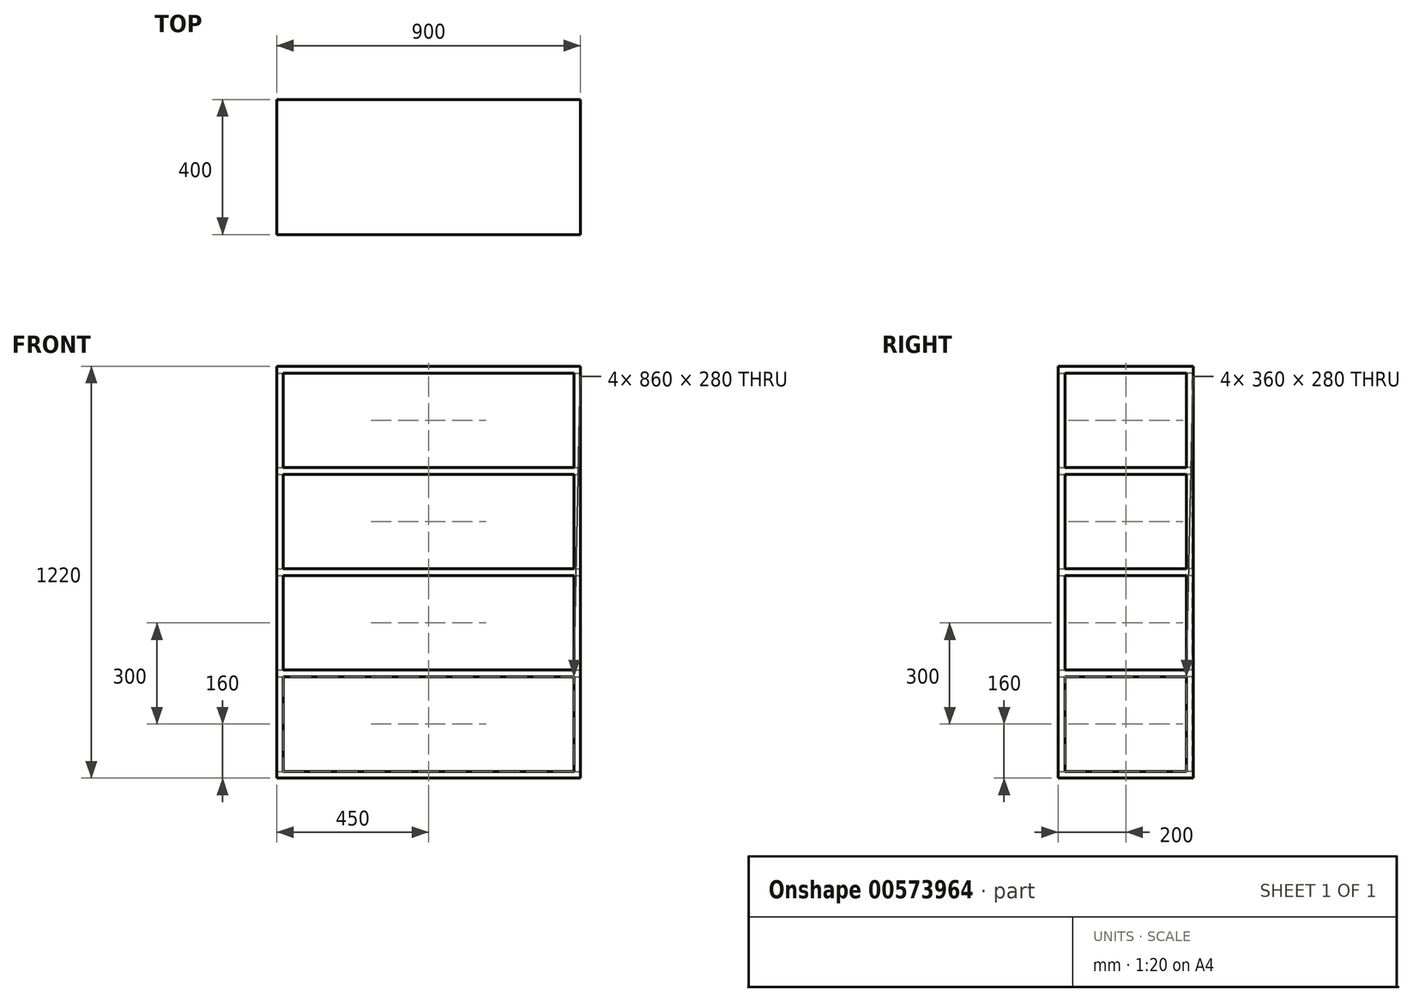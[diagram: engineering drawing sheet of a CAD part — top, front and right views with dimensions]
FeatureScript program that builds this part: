
annotation { "Feature Type Name" : "Feature", "Feature Type Description" : "" }
export const myFeature = defineFeature(function(context is Context, id is Id, definition is map)
    precondition{}
    {
        {
            var Q0;
            Q0=qCreatedBy(makeId("Top.planeOp"),FACE);
            cPlane(context, id + "F0", {"entities" : qUnion([Q0]), "cplaneType" : CPlaneType.OFFSET, "offset" : 300 * mm, "width" : 150 * mm, "height" : 150 * mm});
        }
        {
            var Q0;
            Q0=qCreatedBy(makeId("Top.planeOp"),FACE);
            cPlane(context, id + "F1", {"entities" : qUnion([Q0]), "cplaneType" : CPlaneType.OFFSET, "offset" : 600 * mm, "width" : 150 * mm, "height" : 150 * mm});
        }
        {
            var Q0;
            Q0=qCreatedBy(makeId("Top.planeOp"),FACE);
            cPlane(context, id + "F2", {"entities" : qUnion([Q0]), "cplaneType" : CPlaneType.OFFSET, "offset" : 900 * mm, "width" : 150 * mm, "height" : 150 * mm});
        }
        {
            var Q0;
            Q0=qCreatedBy(makeId("Top.planeOp"),FACE);
            cPlane(context, id + "F3", {"entities" : qUnion([Q0]), "cplaneType" : CPlaneType.OFFSET, "offset" : 1200 * mm, "width" : 150 * mm, "height" : 150 * mm});
        }
        {
            var Q0;
            Q0=qCreatedBy(makeId("Top.planeOp"),FACE);
            var sketch = newSketch(context, id + "F4", { "sketchPlane" : qUnion([Q0])});
            skLineSegment(sketch, "E0.bottom", {"start": v(450, 200) * mm, "end": v(-450, 200) * mm});
            skLineSegment(sketch, "E0.top", {"start": v(450, -200) * mm, "end": v(-450, -200) * mm});
            skLineSegment(sketch, "E0.left", {"start": v(450, 200) * mm, "end": v(450, -200) * mm});
            skLineSegment(sketch, "E0.right", {"start": v(-450, 200) * mm, "end": v(-450, -200) * mm});
            skPoint(sketch, "E0.middle", {"position": v(0, 0) * mm});
            skSolve(sketch);
        }
        {
            var Q0;
            Q0=qCreatedBy(id+"F0.planeOp",FACE);
            var sketch = newSketch(context, id + "F5", { "sketchPlane" : qUnion([Q0])});
            skPoint(sketch, "E1.middle", {"position": v(0, 0) * mm});
            skLineSegment(sketch, "E2", {"start": v(-448, 198) * mm, "end": v(-448, 180) * mm});
            skLineSegment(sketch, "E3", {"start": v(-448, 180) * mm, "end": v(-450, 180) * mm});
            skLineSegment(sketch, "E4", {"start": v(-448, 198) * mm, "end": v(-430, 198) * mm});
            skLineSegment(sketch, "E5", {"start": v(-430, 198) * mm, "end": v(-430, 200) * mm});
            skLineSegment(sketch, "E6", {"start": v(-448, -198) * mm, "end": v(-448, -180) * mm});
            skLineSegment(sketch, "E7", {"start": v(-448, -180) * mm, "end": v(-450, -180) * mm});
            skLineSegment(sketch, "E8", {"start": v(-448, -198) * mm, "end": v(-430, -198) * mm});
            skLineSegment(sketch, "E9", {"start": v(-430, -198) * mm, "end": v(-430, -200) * mm});
            skLineSegment(sketch, "E10", {"start": v(448, -198) * mm, "end": v(448, -180) * mm});
            skLineSegment(sketch, "E11", {"start": v(448, -180) * mm, "end": v(450, -180) * mm});
            skLineSegment(sketch, "E12", {"start": v(430, -198) * mm, "end": v(448, -198) * mm});
            skLineSegment(sketch, "E13", {"start": v(430, -200) * mm, "end": v(430, -198) * mm});
            skLineSegment(sketch, "E14", {"start": v(448, 198) * mm, "end": v(448, 180) * mm});
            skLineSegment(sketch, "E15", {"start": v(448, 180) * mm, "end": v(450, 180) * mm});
            skLineSegment(sketch, "E16", {"start": v(448, 198) * mm, "end": v(430, 198) * mm});
            skLineSegment(sketch, "E17", {"start": v(430, 198) * mm, "end": v(430, 200) * mm});
            skLineSegment(sketch, "E18", {"start": v(430, 200) * mm, "end": v(-430, 200) * mm});
            skLineSegment(sketch, "E19", {"start": v(-450, 180) * mm, "end": v(-450, -180) * mm});
            skLineSegment(sketch, "E20", {"start": v(450, 180) * mm, "end": v(450, -180) * mm});
            skLineSegment(sketch, "E21", {"start": v(430, -200) * mm, "end": v(-430, -200) * mm});
            skSolve(sketch);
        }
        {
            var Q0;
            Q0 = qSketchRegion(id + "F4", true);
            extrude(context, id + "F6", {"entities" : qUnion([Q0]), "depth" : 1220 * mm, "offsetDistance" : 25 * mm});
        }
        {
            var Q0;
            Q0 = qSketchRegion(id + "F5", true);
            extrude(context, id + "F7", {"entities" : qUnion([Q0]), "operationType" : NewBodyOperationType.REMOVE, "oppositeDirection" : true, "depth" : 280 * mm, "offsetDistance" : 25 * mm});
        }
        {
            var Q0;
            Q0=qCreatedBy(id+"F1.planeOp",FACE);
            var sketch = newSketch(context, id + "F8", { "sketchPlane" : qUnion([Q0])});
            skPoint(sketch, "E22.middle", {"position": v(0, 0) * mm});
            skLineSegment(sketch, "E23", {"start": v(-448, 198) * mm, "end": v(-448, 180) * mm});
            skLineSegment(sketch, "E24", {"start": v(-448, 180) * mm, "end": v(-450, 180) * mm});
            skLineSegment(sketch, "E25", {"start": v(-448, 198) * mm, "end": v(-430, 198) * mm});
            skLineSegment(sketch, "E26", {"start": v(-430, 198) * mm, "end": v(-430, 200) * mm});
            skLineSegment(sketch, "E27", {"start": v(-448, -198) * mm, "end": v(-448, -180) * mm});
            skLineSegment(sketch, "E28", {"start": v(-448, -180) * mm, "end": v(-450, -180) * mm});
            skLineSegment(sketch, "E29", {"start": v(-448, -198) * mm, "end": v(-430, -198) * mm});
            skLineSegment(sketch, "E30", {"start": v(-430, -198) * mm, "end": v(-430, -200) * mm});
            skLineSegment(sketch, "E31", {"start": v(448, -198) * mm, "end": v(448, -180) * mm});
            skLineSegment(sketch, "E32", {"start": v(448, -180) * mm, "end": v(450, -180) * mm});
            skLineSegment(sketch, "E33", {"start": v(430, -198) * mm, "end": v(448, -198) * mm});
            skLineSegment(sketch, "E34", {"start": v(430, -200) * mm, "end": v(430, -198) * mm});
            skLineSegment(sketch, "E35", {"start": v(448, 198) * mm, "end": v(448, 180) * mm});
            skLineSegment(sketch, "E36", {"start": v(448, 180) * mm, "end": v(450, 180) * mm});
            skLineSegment(sketch, "E37", {"start": v(448, 198) * mm, "end": v(430, 198) * mm});
            skLineSegment(sketch, "E38", {"start": v(430, 198) * mm, "end": v(430, 200) * mm});
            skLineSegment(sketch, "E39", {"start": v(430, 200) * mm, "end": v(-430, 200) * mm});
            skLineSegment(sketch, "E40", {"start": v(-450, 180) * mm, "end": v(-450, -180) * mm});
            skLineSegment(sketch, "E41", {"start": v(450, 180) * mm, "end": v(450, -180) * mm});
            skLineSegment(sketch, "E42", {"start": v(430, -200) * mm, "end": v(-430, -200) * mm});
            skSolve(sketch);
        }
        {
            var Q0;
            Q0=qCreatedBy(id+"F2.planeOp",FACE);
            var sketch = newSketch(context, id + "F9", { "sketchPlane" : qUnion([Q0])});
            skPoint(sketch, "E43.middle", {"position": v(0, 0) * mm});
            skLineSegment(sketch, "E44", {"start": v(-448, 198) * mm, "end": v(-448, 180) * mm});
            skLineSegment(sketch, "E45", {"start": v(-448, 180) * mm, "end": v(-450, 180) * mm});
            skLineSegment(sketch, "E46", {"start": v(-448, 198) * mm, "end": v(-430, 198) * mm});
            skLineSegment(sketch, "E47", {"start": v(-430, 198) * mm, "end": v(-430, 200) * mm});
            skLineSegment(sketch, "E48", {"start": v(-448, -198) * mm, "end": v(-448, -180) * mm});
            skLineSegment(sketch, "E49", {"start": v(-448, -180) * mm, "end": v(-450, -180) * mm});
            skLineSegment(sketch, "E50", {"start": v(-448, -198) * mm, "end": v(-430, -198) * mm});
            skLineSegment(sketch, "E51", {"start": v(-430, -198) * mm, "end": v(-430, -200) * mm});
            skLineSegment(sketch, "E52", {"start": v(448, -198) * mm, "end": v(448, -180) * mm});
            skLineSegment(sketch, "E53", {"start": v(448, -180) * mm, "end": v(450, -180) * mm});
            skLineSegment(sketch, "E54", {"start": v(430, -198) * mm, "end": v(448, -198) * mm});
            skLineSegment(sketch, "E55", {"start": v(430, -200) * mm, "end": v(430, -198) * mm});
            skLineSegment(sketch, "E56", {"start": v(448, 198) * mm, "end": v(448, 180) * mm});
            skLineSegment(sketch, "E57", {"start": v(448, 180) * mm, "end": v(450, 180) * mm});
            skLineSegment(sketch, "E58", {"start": v(448, 198) * mm, "end": v(430, 198) * mm});
            skLineSegment(sketch, "E59", {"start": v(430, 198) * mm, "end": v(430, 200) * mm});
            skLineSegment(sketch, "E60", {"start": v(430, 200) * mm, "end": v(-430, 200) * mm});
            skLineSegment(sketch, "E61", {"start": v(-450, 180) * mm, "end": v(-450, -180) * mm});
            skLineSegment(sketch, "E62", {"start": v(450, 180) * mm, "end": v(450, -180) * mm});
            skLineSegment(sketch, "E63", {"start": v(430, -200) * mm, "end": v(-430, -200) * mm});
            skSolve(sketch);
        }
        {
            var Q0;
            Q0=qCreatedBy(id+"F3.planeOp",FACE);
            var sketch = newSketch(context, id + "F10", { "sketchPlane" : qUnion([Q0])});
            skPoint(sketch, "E64.middle", {"position": v(0, 0) * mm});
            skLineSegment(sketch, "E65", {"start": v(-448, 198) * mm, "end": v(-448, 180) * mm});
            skLineSegment(sketch, "E66", {"start": v(-448, 180) * mm, "end": v(-450, 180) * mm});
            skLineSegment(sketch, "E67", {"start": v(-448, 198) * mm, "end": v(-430, 198) * mm});
            skLineSegment(sketch, "E68", {"start": v(-430, 198) * mm, "end": v(-430, 200) * mm});
            skLineSegment(sketch, "E69", {"start": v(-448, -198) * mm, "end": v(-448, -180) * mm});
            skLineSegment(sketch, "E70", {"start": v(-448, -180) * mm, "end": v(-450, -180) * mm});
            skLineSegment(sketch, "E71", {"start": v(-448, -198) * mm, "end": v(-430, -198) * mm});
            skLineSegment(sketch, "E72", {"start": v(-430, -198) * mm, "end": v(-430, -200) * mm});
            skLineSegment(sketch, "E73", {"start": v(448, -198) * mm, "end": v(448, -180) * mm});
            skLineSegment(sketch, "E74", {"start": v(448, -180) * mm, "end": v(450, -180) * mm});
            skLineSegment(sketch, "E75", {"start": v(430, -198) * mm, "end": v(448, -198) * mm});
            skLineSegment(sketch, "E76", {"start": v(430, -200) * mm, "end": v(430, -198) * mm});
            skLineSegment(sketch, "E77", {"start": v(448, 198) * mm, "end": v(448, 180) * mm});
            skLineSegment(sketch, "E78", {"start": v(448, 180) * mm, "end": v(450, 180) * mm});
            skLineSegment(sketch, "E79", {"start": v(448, 198) * mm, "end": v(430, 198) * mm});
            skLineSegment(sketch, "E80", {"start": v(430, 198) * mm, "end": v(430, 200) * mm});
            skLineSegment(sketch, "E81", {"start": v(430, 200) * mm, "end": v(-430, 200) * mm});
            skLineSegment(sketch, "E82", {"start": v(-450, 180) * mm, "end": v(-450, -180) * mm});
            skLineSegment(sketch, "E83", {"start": v(450, 180) * mm, "end": v(450, -180) * mm});
            skLineSegment(sketch, "E84", {"start": v(430, -200) * mm, "end": v(-430, -200) * mm});
            skSolve(sketch);
        }
        {
            var Q0;
            Q0 = qSketchRegion(id + "F8", true);
            extrude(context, id + "F11", {"entities" : qUnion([Q0]), "operationType" : NewBodyOperationType.REMOVE, "oppositeDirection" : true, "depth" : 280 * mm, "offsetDistance" : 25 * mm});
        }
        {
            var Q0;
            Q0 = qSketchRegion(id + "F9", true);
            extrude(context, id + "F12", {"entities" : qUnion([Q0]), "operationType" : NewBodyOperationType.REMOVE, "oppositeDirection" : true, "depth" : 280 * mm, "offsetDistance" : 25 * mm});
        }
        {
            var Q0;
            Q0 = qSketchRegion(id + "F10", true);
            extrude(context, id + "F13", {"entities" : qUnion([Q0]), "operationType" : NewBodyOperationType.REMOVE, "oppositeDirection" : true, "depth" : 280 * mm, "offsetDistance" : 25 * mm});
        }
    });
